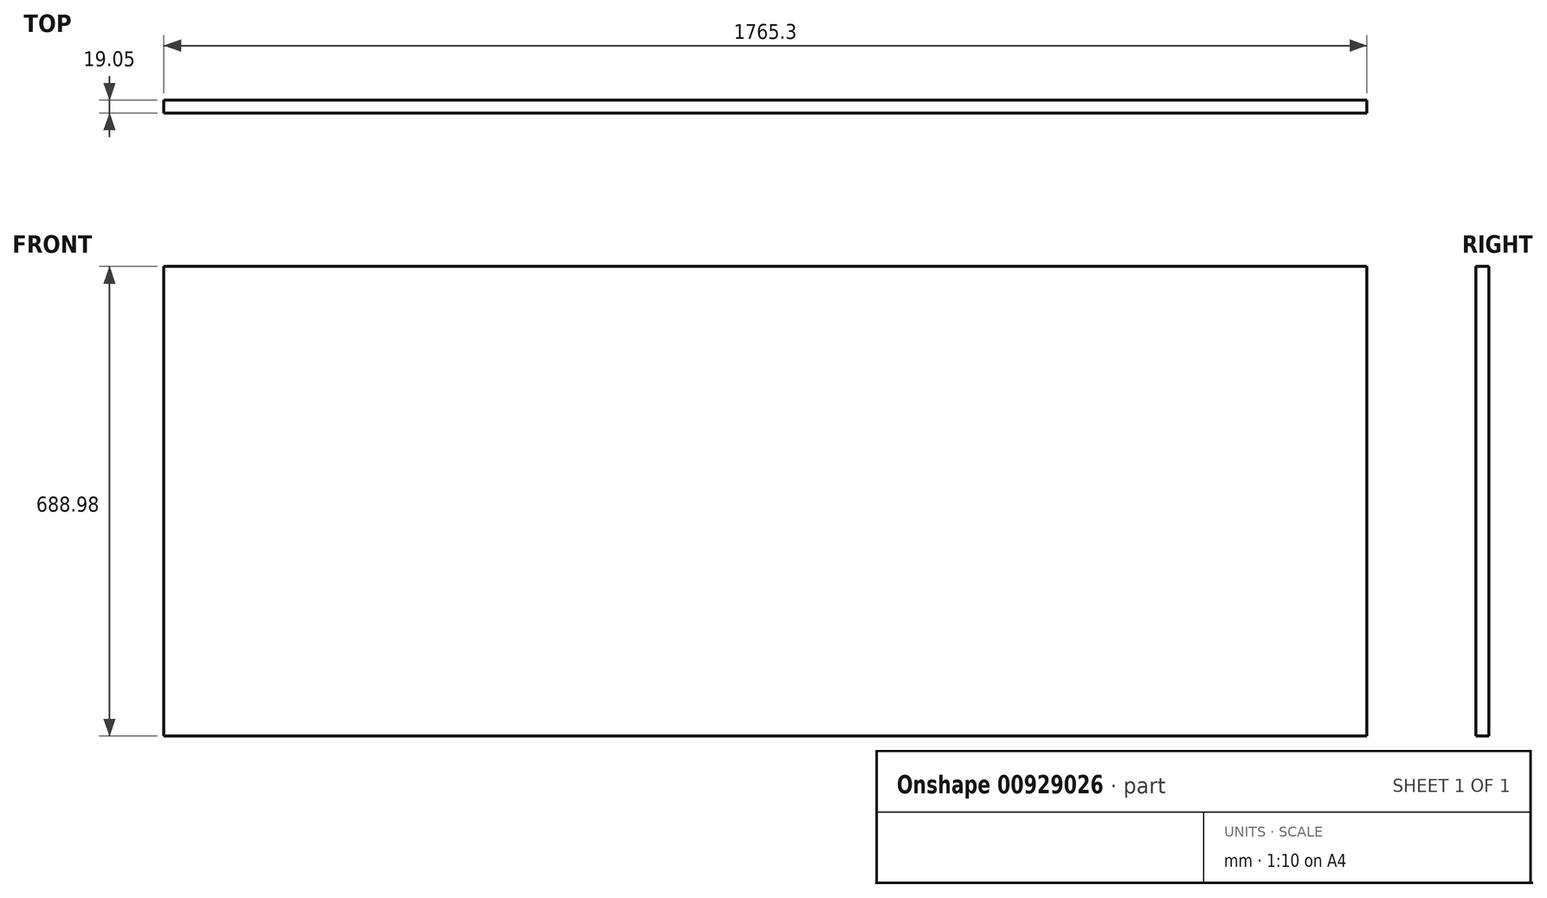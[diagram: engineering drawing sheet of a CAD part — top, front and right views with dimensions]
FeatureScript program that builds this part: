
annotation { "Feature Type Name" : "Feature", "Feature Type Description" : "" }
export const myFeature = defineFeature(function(context is Context, id is Id, definition is map)
    precondition{}
    {
        {
            var Q0;
            Q0=qCreatedBy(makeId("Front.planeOp"),FACE);
            var sketch = newSketch(context, id + "F0", { "sketchPlane" : qUnion([Q0])});
            skLineSegment(sketch, "E0.bottom", {"start": v(882.65, 344.49) * mm, "end": v(-882.65, 344.49) * mm});
            skLineSegment(sketch, "E0.top", {"start": v(882.65, -344.49) * mm, "end": v(-882.65, -344.49) * mm});
            skLineSegment(sketch, "E0.left", {"start": v(882.65, 344.49) * mm, "end": v(882.65, -344.49) * mm});
            skLineSegment(sketch, "E0.right", {"start": v(-882.65, 344.49) * mm, "end": v(-882.65, -344.49) * mm});
            skPoint(sketch, "E0.middle", {"position": v(0, 0) * mm});
            skSolve(sketch);
        }
        {
            var Q0;
            Q0=makeQuery(id+"F0.imprint","IMPRINT",FACE,{"disambiguationData":[TD([[makeQuery(id+"F0.imprint","IMPRINT",EDGE,{"derivedFrom":sQuery(id+"F0.wireOp",EDGE,"E0.bottom")}),1.0]])]});
            extrude(context, id + "F1", {"entities" : qUnion([Q0]), "depth" : 19.05 * mm, "offsetDistance" : 25.4 * mm});
        }
    });
